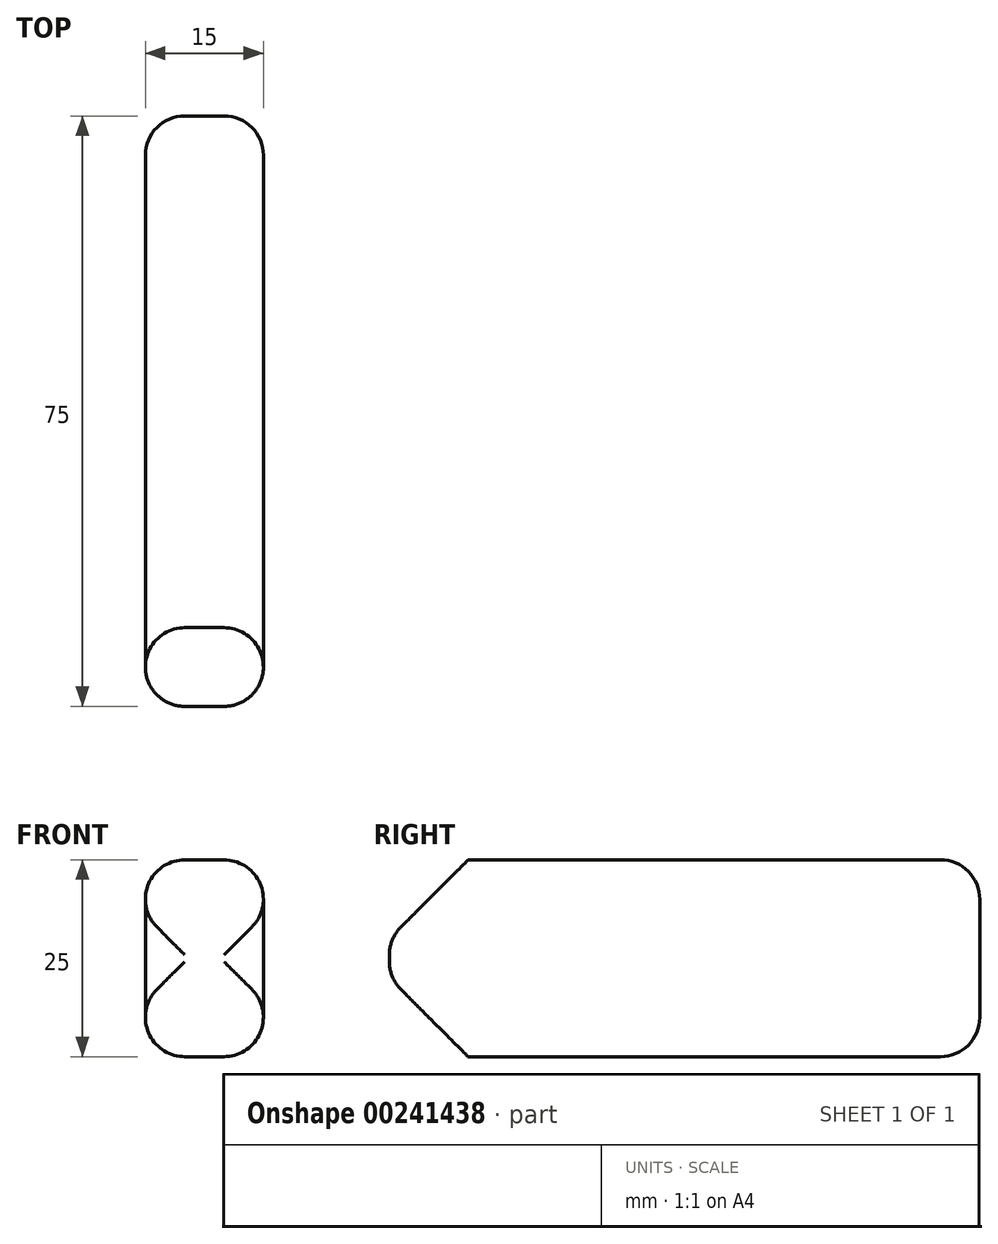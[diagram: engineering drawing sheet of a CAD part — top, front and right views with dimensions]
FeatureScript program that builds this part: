
annotation { "Feature Type Name" : "Feature", "Feature Type Description" : "" }
export const myFeature = defineFeature(function(context is Context, id is Id, definition is map)
    precondition{}
    {
        {
            var Q0;
            Q0=qCreatedBy(makeId("Right.planeOp"),FACE);
            var sketch = newSketch(context, id + "F0", { "sketchPlane" : qUnion([Q0])});
            skLineSegment(sketch, "E0.bottom", {"start": v(-37.5, 12.5) * mm, "end": v(37.5, 12.5) * mm});
            skLineSegment(sketch, "E0.top", {"start": v(-37.5, -12.5) * mm, "end": v(37.5, -12.5) * mm});
            skLineSegment(sketch, "E0.left", {"start": v(-37.5, 12.5) * mm, "end": v(-37.5, -12.5) * mm});
            skLineSegment(sketch, "E0.right", {"start": v(37.5, 12.5) * mm, "end": v(37.5, -12.5) * mm});
            skPoint(sketch, "E0.middle", {"position": v(0, 0) * mm});
            skSolve(sketch);
        }
        {
            var Q0;
            Q0 = qSketchRegion(id + "F0", true);
            extrude(context, id + "F1", {"entities" : qUnion([Q0]), "depth" : 15 * mm});
        }
        {
            var Q0;
            Q0=makeQuery(id+"F1.opExtrude","SWEPT_EDGE",EDGE,{"disambiguationData":[OSD([sQuery(id+"F0.wireOp",EDGE,"E0.bottom"),sQuery(id+"F0.wireOp",EDGE,"E0.left")])]});
            chamfer(context, id + "F2", {"entities" : qUnion([Q0]), "width" : 10 * mm, "tangentPropagation" : true});
        }
        {
            var Q0;
            Q0=makeQuery(id+"F1.opExtrude","SWEPT_EDGE",EDGE,{"disambiguationData":[OSD([sQuery(id+"F0.wireOp",EDGE,"E0.top"),sQuery(id+"F0.wireOp",EDGE,"E0.left")])]});
            chamfer(context, id + "F3", {"entities" : qUnion([Q0]), "width" : 10 * mm});
        }
        {
            var Q0;
            Q0=makeQuery(id+"F1.opExtrude","CAP_EDGE",EDGE,{"disambiguationData":[OSD([sQuery(id+"F0.wireOp",EDGE,"E0.bottom")])],"isStart":false});
            var Q1;
            Q1=makeQuery(id+"F1.opExtrude","CAP_EDGE",EDGE,{"disambiguationData":[OSD([sQuery(id+"F0.wireOp",EDGE,"E0.bottom")])],"isStart":true});
            var Q2;
            Q2=makeQuery(id+"F1.opExtrude","CAP_EDGE",EDGE,{"disambiguationData":[OSD([sQuery(id+"F0.wireOp",EDGE,"E0.top")])],"isStart":false});
            var Q3;
            Q3=makeQuery(id+"F1.opExtrude","CAP_EDGE",EDGE,{"disambiguationData":[OSD([sQuery(id+"F0.wireOp",EDGE,"E0.top")])],"isStart":true});
            fillet(context, id + "F4", {"entities" : qUnion([Q0, Q1, Q2, Q3]), "radius" : 5 * mm, "tangentPropagation" : true, "allowEdgeOverflow" : false});
        }
        {
            var Q0;
            Q0=makeQuery(id+"F1.opExtrude","SWEPT_FACE",FACE,{"disambiguationData":[OSD([sQuery(id+"F0.wireOp",EDGE,"E0.right")])]});
            fillet(context, id + "F5", {"entities" : qUnion([Q0]), "radius" : 5 * mm, "tangentPropagation" : true, "allowEdgeOverflow" : false});
        }
        {
            var Q0;
            Q0=makeQuery(id+"F1.opExtrude","SWEPT_FACE",FACE,{"disambiguationData":[OSD([sQuery(id+"F0.wireOp",EDGE,"E0.left")])]});
            fillet(context, id + "F6", {"entities" : qUnion([Q0]), "radius" : 5 * mm, "tangentPropagation" : true, "allowEdgeOverflow" : false});
        }
    });
